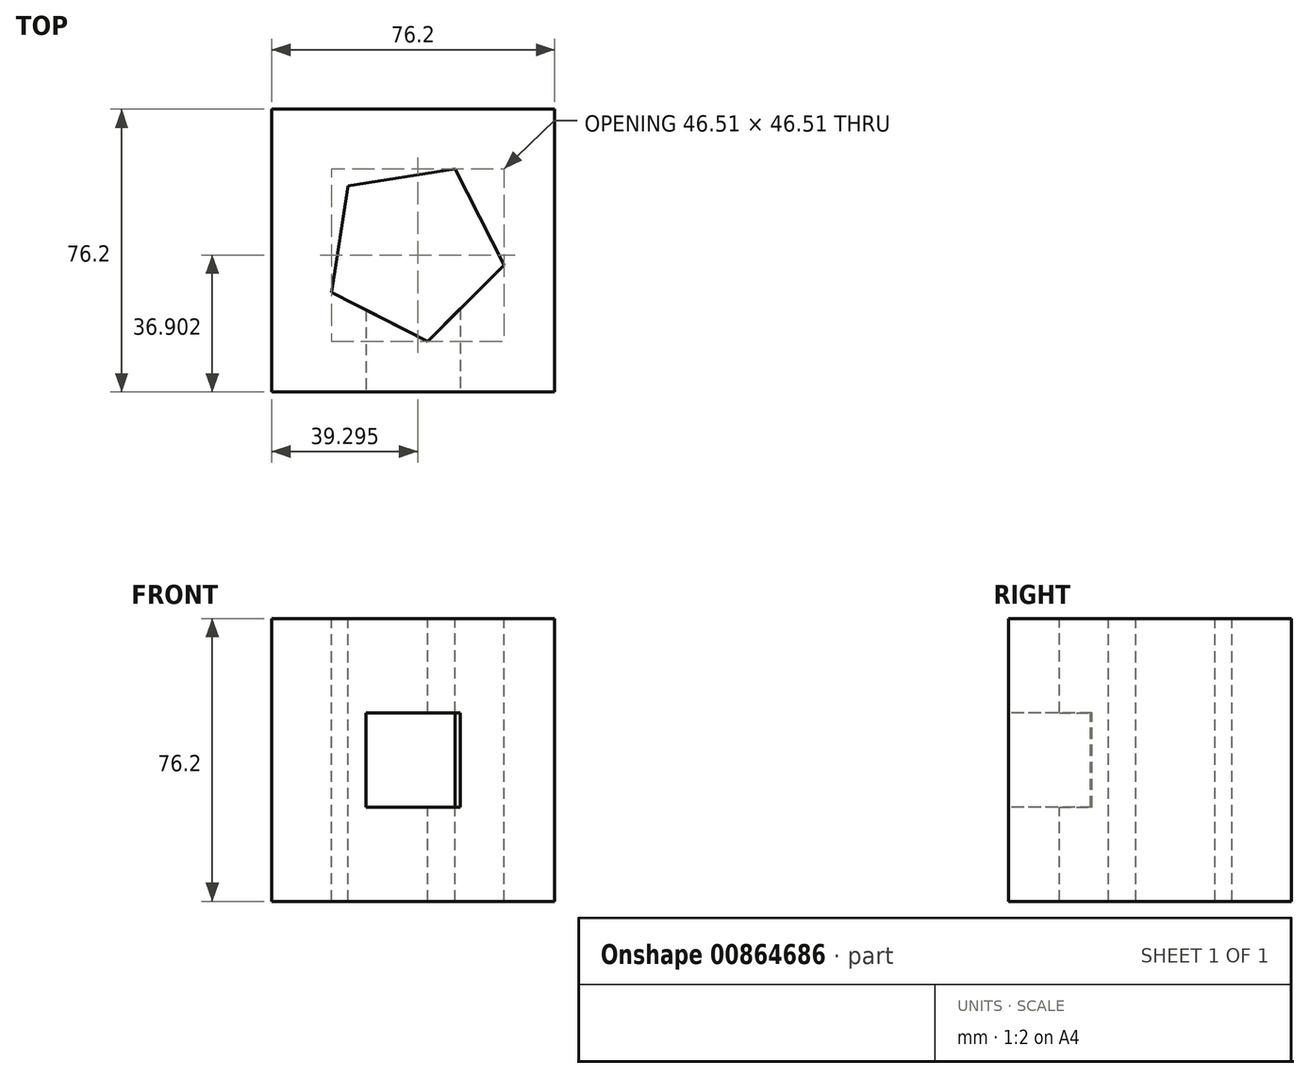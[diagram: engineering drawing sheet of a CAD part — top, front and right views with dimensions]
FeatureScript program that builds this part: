
annotation { "Feature Type Name" : "Feature", "Feature Type Description" : "" }
export const myFeature = defineFeature(function(context is Context, id is Id, definition is map)
    precondition{}
    {
        {
            var Q0;
            Q0=qCreatedBy(makeId("Top.planeOp"),FACE);
            var sketch = newSketch(context, id + "F0", { "sketchPlane" : qUnion([Q0])});
            skLineSegment(sketch, "E0.bottom", {"start": v(0, 0) * mm, "end": v(76.2, 0) * mm});
            skLineSegment(sketch, "E0.top", {"start": v(0, 76.2) * mm, "end": v(76.2, 76.2) * mm});
            skLineSegment(sketch, "E0.left", {"start": v(0, 0) * mm, "end": v(0, 76.2) * mm});
            skLineSegment(sketch, "E0.right", {"start": v(76.2, 0) * mm, "end": v(76.2, 76.2) * mm});
            skSolve(sketch);
        }
        {
            var Q0;
            Q0 = qSketchRegion(id + "F0", true);
            extrude(context, id + "F1", {"entities" : qUnion([Q0]), "depth" : 76.2 * mm, "offsetDistance" : 25.4 * mm});
        }
        {
            var Q0;
            Q0=makeQuery(id+"F1.opExtrude","CAP_FACE",FACE,{"disambiguationData":[OSD([sQuery(id+"F0.wireOp",EDGE,"E0.bottom"),sQuery(id+"F0.wireOp",EDGE,"E0.top"),sQuery(id+"F0.wireOp",EDGE,"E0.left"),sQuery(id+"F0.wireOp",EDGE,"E0.right")])],"isStart":false});
            var sketch = newSketch(context, id + "F2", { "sketchPlane" : qUnion([Q0])});
            skCircle(sketch, "E1.cCircle", {"center": v(38.1, 38.1) * mm, "radius": 20.03 * mm, "construction": true});
            skLineSegment(sketch, "E1.0", {"start": v(62.55, 34.22) * mm, "end": v(41.97, 13.65) * mm});
            skLineSegment(sketch, "E1.1", {"start": v(41.97, 13.65) * mm, "end": v(16.04, 26.86) * mm});
            skLineSegment(sketch, "E1.2", {"start": v(16.04, 26.86) * mm, "end": v(20.6, 55.6) * mm});
            skLineSegment(sketch, "E1.3", {"start": v(20.6, 55.6) * mm, "end": v(49.34, 60.16) * mm});
            skLineSegment(sketch, "E1.4", {"start": v(49.34, 60.16) * mm, "end": v(62.55, 34.22) * mm});
            skPoint(sketch, "E1.0.midPoint", {"position": v(52.26, 23.94) * mm});
            skSolve(sketch);
        }
        {
            var Q0;
            Q0=makeQuery(id+"F2.imprint","IMPRINT",FACE,{"disambiguationData":[TD([[makeQuery(id+"F2.imprint","IMPRINT",EDGE,{"derivedFrom":sQuery(id+"F2.wireOp",EDGE,"E1.0")}),-1.0]])]});
            extrude(context, id + "F3", {"entities" : qUnion([Q0]), "operationType" : NewBodyOperationType.REMOVE, "endBound" : BoundingType.THROUGH_ALL, "oppositeDirection" : true, "depth" : 25.4 * mm, "offsetDistance" : 25.4 * mm});
        }
        {
            var Q0;
            Q0=makeQuery(id+"F1.opExtrude","SWEPT_FACE",FACE,{"disambiguationData":[OSD([sQuery(id+"F0.wireOp",EDGE,"E0.bottom")])]});
            var sketch = newSketch(context, id + "F4", { "sketchPlane" : qUnion([Q0])});
            skLineSegment(sketch, "E2.0", {"start": v(25.4, 50.8) * mm, "end": v(25.4, 25.4) * mm});
            skLineSegment(sketch, "E2.1", {"start": v(25.4, 50.8) * mm, "end": v(50.8, 50.8) * mm});
            skLineSegment(sketch, "E2.2", {"start": v(50.8, 50.8) * mm, "end": v(50.8, 25.4) * mm});
            skLineSegment(sketch, "E2.3", {"start": v(25.4, 25.4) * mm, "end": v(50.8, 25.4) * mm});
            skSolve(sketch);
        }
        {
            var Q0;
            Q0=makeQuery(id+"F4.imprint","IMPRINT",FACE,{"disambiguationData":[TD([[makeQuery(id+"F4.imprint","IMPRINT",EDGE,{"derivedFrom":sQuery(id+"F4.wireOp",EDGE,"E2.0")}),1.0]])]});
            extrude(context, id + "F5", {"entities" : qUnion([Q0]), "operationType" : NewBodyOperationType.REMOVE, "oppositeDirection" : true, "depth" : 12.7 * mm, "offsetDistance" : 25.4 * mm});
        }
        {
            var Q0;
            Q0=makeQuery(id+"F4.imprint","IMPRINT",FACE,{"disambiguationData":[TD([[makeQuery(id+"F4.imprint","IMPRINT",EDGE,{"derivedFrom":sQuery(id+"F4.wireOp",EDGE,"E2.0")}),1.0]])]});
            extrude(context, id + "F6", {"entities" : qUnion([Q0]), "operationType" : NewBodyOperationType.REMOVE, "oppositeDirection" : true, "depth" : 25.4 * mm, "offsetDistance" : 25.4 * mm});
        }
    });
